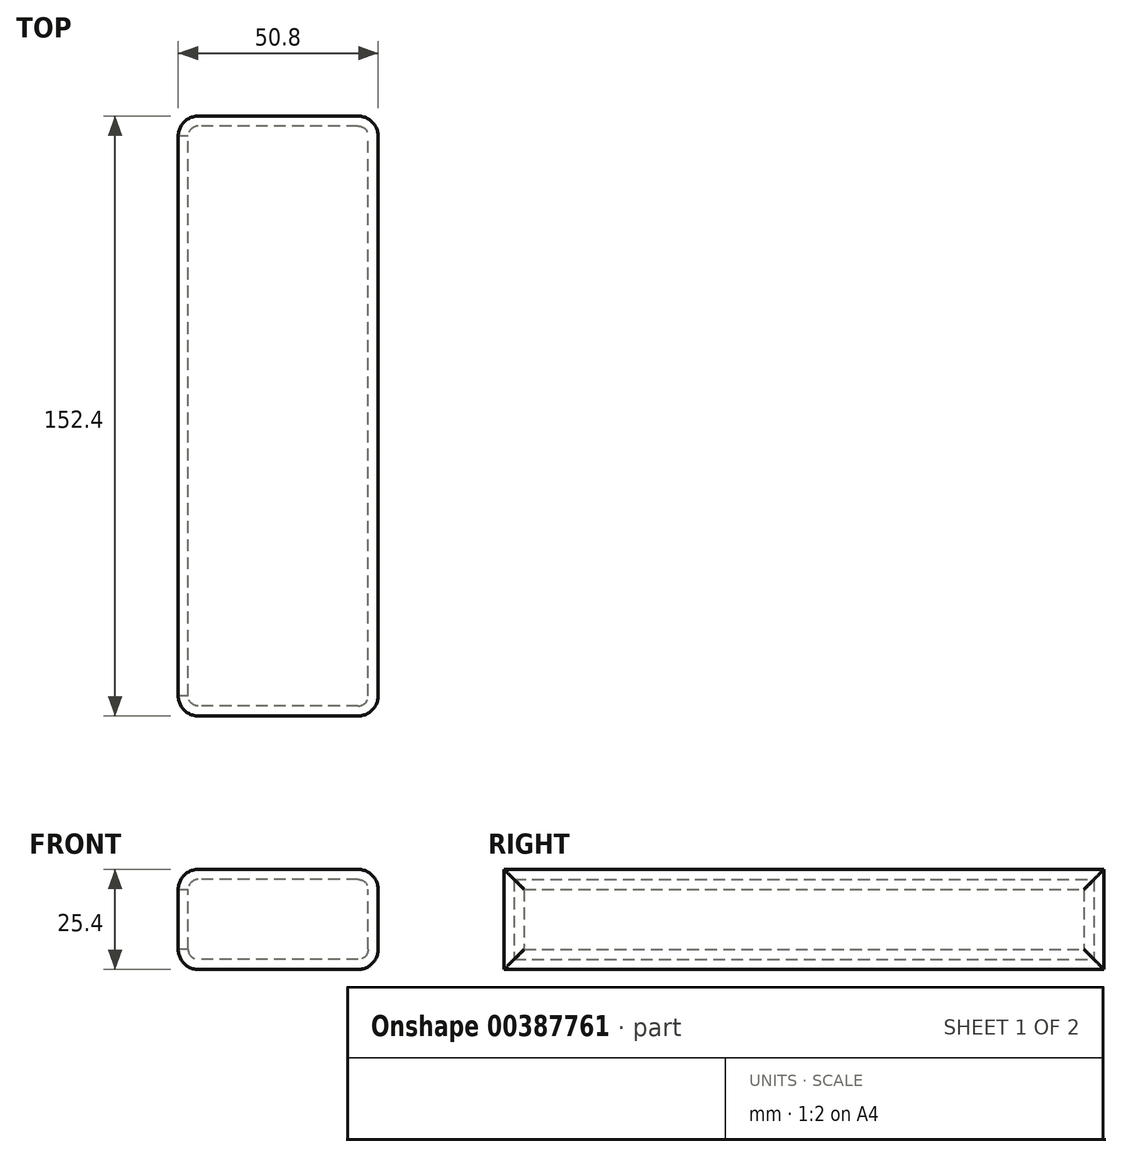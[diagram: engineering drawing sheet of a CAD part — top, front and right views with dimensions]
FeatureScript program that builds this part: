
annotation { "Feature Type Name" : "Feature", "Feature Type Description" : "" }
export const myFeature = defineFeature(function(context is Context, id is Id, definition is map)
    precondition{}
    {
        {
            var Q0;
            Q0=qCreatedBy(makeId("Top.planeOp"),FACE);
            var sketch = newSketch(context, id + "F0", { "sketchPlane" : qUnion([Q0])});
            skLineSegment(sketch, "E0.bottom", {"start": v(25.4, -76.2) * mm, "end": v(-25.4, -76.2) * mm});
            skLineSegment(sketch, "E0.top", {"start": v(25.4, 76.2) * mm, "end": v(-25.4, 76.2) * mm});
            skLineSegment(sketch, "E0.left", {"start": v(25.4, -76.2) * mm, "end": v(25.4, 76.2) * mm});
            skLineSegment(sketch, "E0.right", {"start": v(-25.4, -76.2) * mm, "end": v(-25.4, 76.2) * mm});
            skPoint(sketch, "E0.middle", {"position": v(0, 0) * mm});
            skSolve(sketch);
        }
        {
            var Q0;
            Q0 = qSketchRegion(id + "F0", true);
            extrude(context, id + "F1", {"entities" : qUnion([Q0]), "depth" : 25.4 * mm});
        }
        {
            var Q0;
            Q0=makeQuery(id+"F1.opExtrude","SWEPT_EDGE",EDGE,{"disambiguationData":[OSD([sQuery(id+"F0.wireOp",EDGE,"E0.top"),sQuery(id+"F0.wireOp",EDGE,"E0.right")])]});
            var Q1;
            Q1=makeQuery(id+"F1.opExtrude","SWEPT_EDGE",EDGE,{"disambiguationData":[OSD([sQuery(id+"F0.wireOp",EDGE,"E0.top"),sQuery(id+"F0.wireOp",EDGE,"E0.left")])]});
            var Q2;
            Q2=makeQuery(id+"F1.opExtrude","SWEPT_EDGE",EDGE,{"disambiguationData":[OSD([sQuery(id+"F0.wireOp",EDGE,"E0.bottom"),sQuery(id+"F0.wireOp",EDGE,"E0.right")])]});
            var Q3;
            Q3=makeQuery(id+"F1.opExtrude","SWEPT_EDGE",EDGE,{"disambiguationData":[OSD([sQuery(id+"F0.wireOp",EDGE,"E0.bottom"),sQuery(id+"F0.wireOp",EDGE,"E0.left")])]});
            var Q4;
            Q4=makeQuery(id+"F1.opExtrude","CAP_EDGE",EDGE,{"disambiguationData":[OSD([sQuery(id+"F0.wireOp",EDGE,"E0.left")])],"isStart":false});
            var Q5;
            Q5=makeQuery(id+"F1.opExtrude","CAP_EDGE",EDGE,{"disambiguationData":[OSD([sQuery(id+"F0.wireOp",EDGE,"E0.left")])],"isStart":true});
            var Q6;
            Q6=makeQuery(id+"F1.opExtrude","CAP_EDGE",EDGE,{"disambiguationData":[OSD([sQuery(id+"F0.wireOp",EDGE,"E0.right")])],"isStart":false});
            var Q7;
            Q7=makeQuery(id+"F1.opExtrude","CAP_EDGE",EDGE,{"disambiguationData":[OSD([sQuery(id+"F0.wireOp",EDGE,"E0.right")])],"isStart":true});
            fillet(context, id + "F2", {"entities" : qUnion([Q0, Q1, Q2, Q3, Q4, Q5, Q6, Q7]), "radius" : 5.08 * mm, "tangentPropagation" : true, "allowEdgeOverflow" : false});
        }
        {
            var Q0;
            Q0=makeQuery(id+"F1.opExtrude","SWEPT_FACE",FACE,{"disambiguationData":[OSD([sQuery(id+"F0.wireOp",EDGE,"E0.right")])]});
            shell(context, id + "F3", {"entities" : qUnion([Q0]), "thickness" : 2.54 * mm});
        }
    });
